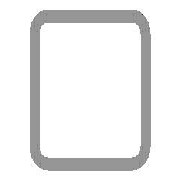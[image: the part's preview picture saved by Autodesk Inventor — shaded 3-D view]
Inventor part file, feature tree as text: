
AUTODESK INVENTOR PART (.ipt)
format: ipt  version: 2025 (Build 290162010, 162A)  size: 134,656 bytes
history: native  units: mm (DEFAULTED — no unit token found)
features: other x4, sketch x1, plane x1
ambient origin geometry x8: Origin, YZ Plane, XZ Plane, XY Plane, X Axis, Y Axis, Z Axis, Center Point
bodies: Solid1 (feature_tree), Body (feature_tree)
feature tree (6):
  parser-record x1  (decoder bookkeeping rows leaked as tree rows — omitted from the tree; the rows remain in map.json)
  other  "Driven Length"
  other  "Start Plane"
  other  "End Plane"
  sketch  "Sketch3"  dims[d3=700.0mm d4=0.0mm d7=6.0mm d9=80.0mm d11=80.0mm d12=3.0mm d13=-0.0mm d14=700.0mm d15=40.0mm d16=40.0mm d17=90.0deg d18=700.0mm]
  plane  "Work Plane3"
